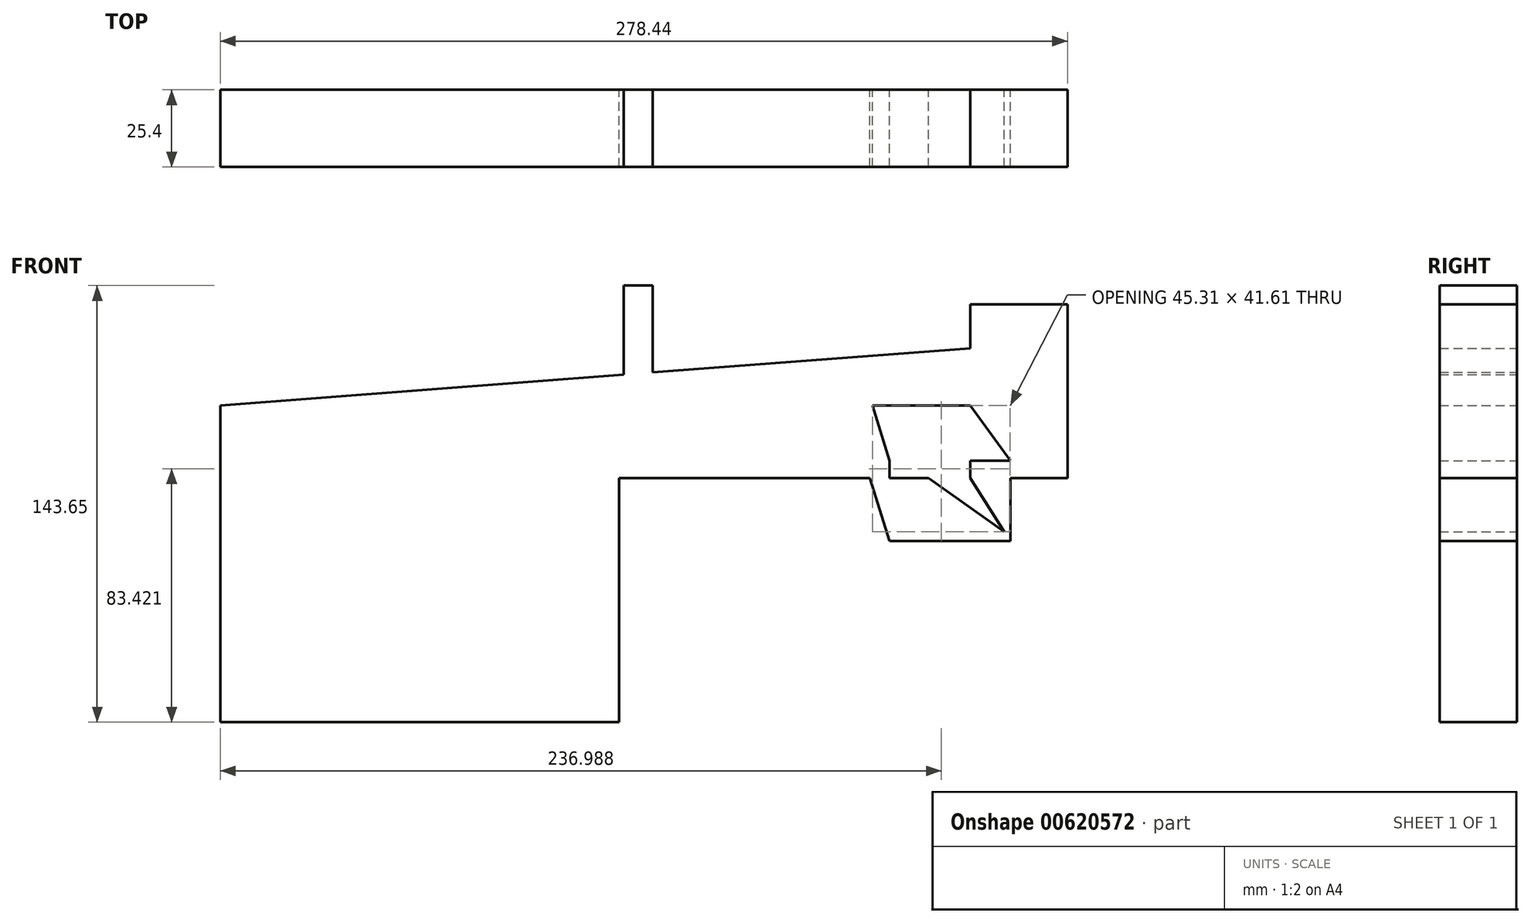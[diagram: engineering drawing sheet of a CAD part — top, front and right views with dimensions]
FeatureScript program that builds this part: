
annotation { "Feature Type Name" : "Feature", "Feature Type Description" : "" }
export const myFeature = defineFeature(function(context is Context, id is Id, definition is map)
    precondition{}
    {
        {
            var Q0;
            Q0=qCreatedBy(makeId("Front.planeOp"),FACE);
            var sketch = newSketch(context, id + "F0", { "sketchPlane" : qUnion([Q0])});
            skLineSegment(sketch, "E0.bottom", {"start": v(53.1, 23.92) * mm, "end": v(-62.4, 23.92) * mm});
            skLineSegment(sketch, "E0.top", {"start": v(53.1, 0) * mm, "end": v(-62.4, 0) * mm});
            skLineSegment(sketch, "E0.left", {"start": v(53.1, 23.92) * mm, "end": v(53.1, 0) * mm});
            skLineSegment(sketch, "E0.right", {"start": v(-62.4, 23.92) * mm, "end": v(-62.4, 0) * mm});
            skLineSegment(sketch, "E1.bottom", {"start": v(85.02, 57.14) * mm, "end": v(53.1, 57.14) * mm});
            skLineSegment(sketch, "E1.top", {"start": v(85.02, 0) * mm, "end": v(53.1, 0) * mm});
            skLineSegment(sketch, "E1.left", {"start": v(85.02, 57.14) * mm, "end": v(85.02, 0) * mm});
            skLineSegment(sketch, "E1.right", {"start": v(53.1, 57.14) * mm, "end": v(53.1, 0) * mm});
            skLineSegment(sketch, "E2.bottom", {"start": v(-51.3, 63.35) * mm, "end": v(-60.9, 63.35) * mm});
            skLineSegment(sketch, "E2.top", {"start": v(-51.3, 0) * mm, "end": v(-60.9, 0) * mm});
            skLineSegment(sketch, "E2.left", {"start": v(-60.9, 63.35) * mm, "end": v(-60.9, 0) * mm});
            skLineSegment(sketch, "E2.right", {"start": v(-51.3, 63.35) * mm, "end": v(-51.3, 0) * mm});
            skLineSegment(sketch, "E3.bottom", {"start": v(-62.4, 23.92) * mm, "end": v(-193.42, 23.92) * mm});
            skLineSegment(sketch, "E3.top", {"start": v(-62.4, -80.3) * mm, "end": v(-193.42, -80.3) * mm});
            skLineSegment(sketch, "E3.left", {"start": v(-62.4, 23.92) * mm, "end": v(-62.4, -80.3) * mm});
            skLineSegment(sketch, "E3.right", {"start": v(-193.42, 23.92) * mm, "end": v(-193.42, -80.3) * mm});
            skLineSegment(sketch, "E4.bottom", {"start": v(53.1, 0) * mm, "end": v(53.1, 0) * mm});
            skLineSegment(sketch, "E4.top", {"start": v(53.1, 23.92) * mm, "end": v(53.1, 23.92) * mm});
            skLineSegment(sketch, "E4.left", {"start": v(53.1, 0) * mm, "end": v(53.1, 23.92) * mm});
            skLineSegment(sketch, "E4.right", {"start": v(53.1, 0) * mm, "end": v(53.1, 23.92) * mm});
            skLineSegment(sketch, "E5.bottom", {"start": v(66.22, -20.75) * mm, "end": v(26.48, -20.75) * mm});
            skLineSegment(sketch, "E5.top", {"start": v(66.22, 5.76) * mm, "end": v(26.48, 5.76) * mm});
            skLineSegment(sketch, "E5.left", {"start": v(66.22, -20.75) * mm, "end": v(66.22, 5.76) * mm});
            skLineSegment(sketch, "E5.right", {"start": v(26.48, -20.75) * mm, "end": v(26.48, 5.76) * mm});
            skLineSegment(sketch, "E6", {"start": v(53.1, 23.92) * mm, "end": v(66.22, 5.76) * mm});
            skLineSegment(sketch, "E7", {"start": v(53.1, 0) * mm, "end": v(66.22, -20.75) * mm});
            skLineSegment(sketch, "E8", {"start": v(26.48, 5.76) * mm, "end": v(20.91, 23.92) * mm});
            skLineSegment(sketch, "E9", {"start": v(26.48, -20.75) * mm, "end": v(20.12, 0) * mm});
            skLineSegment(sketch, "E10", {"start": v(20.12, 0) * mm, "end": v(20.91, 23.92) * mm});
            skLineSegment(sketch, "E11", {"start": v(622.58, 85.2) * mm, "end": v(727.57, 94.21) * mm});
            skLineSegment(sketch, "E12", {"start": v(727.57, 94.21) * mm, "end": v(-193.42, 23.92) * mm});
            skLineSegment(sketch, "E13", {"start": v(404.1, 23.92) * mm, "end": v(727.57, 94.21) * mm});
            skPoint(sketch, "E13.startSnap0", {"position": v(-4.64, 23.92) * mm});
            skLineSegment(sketch, "E14", {"start": v(760.17, -510.42) * mm, "end": v(26.52, 9.06) * mm});
            skSolve(sketch);
        }
        {
            var Q0;
            Q0 = qSketchRegion(id + "F0", true);
            extrude(context, id + "F1", {"entities" : qUnion([Q0]), "depth" : 25.4 * mm, "offsetDistance" : 25.4 * mm});
        }
    });
